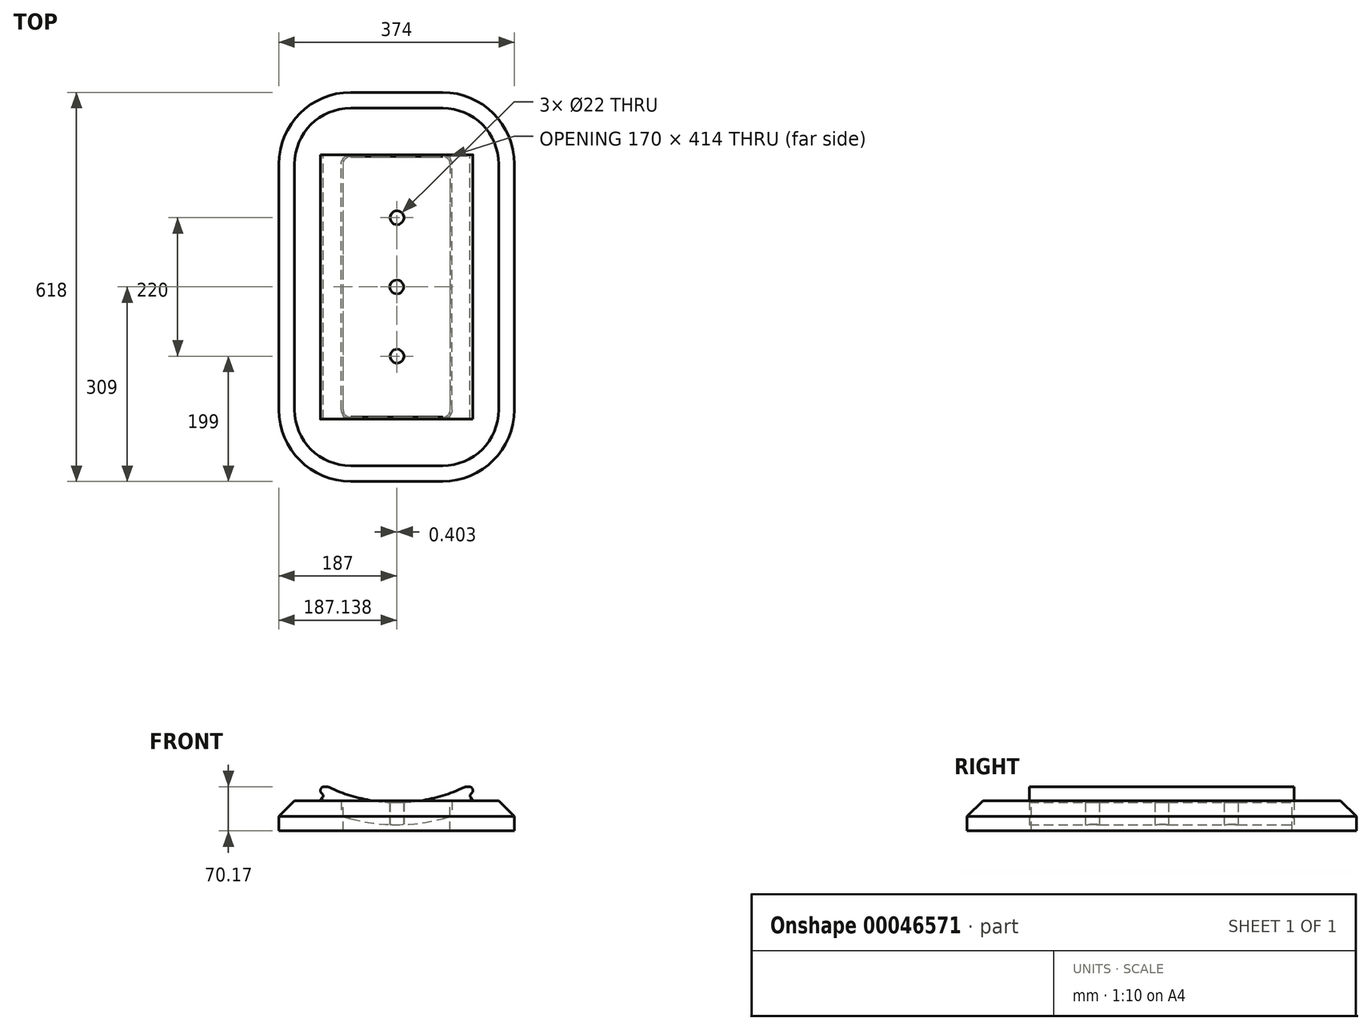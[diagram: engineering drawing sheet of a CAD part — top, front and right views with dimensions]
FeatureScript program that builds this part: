
annotation { "Feature Type Name" : "Feature", "Feature Type Description" : "" }
export const myFeature = defineFeature(function(context is Context, id is Id, definition is map)
    precondition{}
    {
        {
            var Q0;
            Q0=qCreatedBy(makeId("Front.planeOp"),FACE);
            var sketch = newSketch(context, id + "F0", { "sketchPlane" : qUnion([Q0])});
            skArc(sketch, "E0", {"start": v(0, -251.5) * mm, "mid": v(55, -245.41) * mm, "end": v(107.33, -227.45) * mm});
            skLineSegment(sketch, "E1", {"start": v(0, 0) * mm, "end": v(0, -251.5) * mm, "construction": true});
            skLineSegment(sketch, "E2", {"start": v(88, -248.66) * mm, "end": v(88, -272.86) * mm});
            skArc(sketch, "E3", {"start": v(0, -286.7) * mm, "mid": v(44.54, -283.22) * mm, "end": v(88, -272.86) * mm});
            skLineSegment(sketch, "E4", {"start": v(88, -248.66) * mm, "end": v(121, -248.66) * mm});
            skLineSegment(sketch, "E5", {"start": v(121, -248.66) * mm, "end": v(117.68, -243.92) * mm});
            skLineSegment(sketch, "E6", {"start": v(118.25, -237.52) * mm, "end": v(119.62, -236.15) * mm});
            skLineSegment(sketch, "E7", {"start": v(120.65, -230.6) * mm, "end": v(120.16, -229.47) * mm});
            skLineSegment(sketch, "E8", {"start": v(115.58, -226.5) * mm, "end": v(111.6, -226.5) * mm});
            skPoint(sketch, "E9.visualSharp", {"position": v(118.84, -226.5) * mm});
            skArc(sketch, "E9.filletArc", {"start": v(120.16, -229.47) * mm, "mid": v(118.31, -227.3) * mm, "end": v(115.58, -226.5) * mm});
            skPoint(sketch, "E10.visualSharp", {"position": v(122.04, -233.73) * mm});
            skArc(sketch, "E10.filletArc", {"start": v(119.62, -236.15) * mm, "mid": v(121, -233.53) * mm, "end": v(120.65, -230.6) * mm});
            skPoint(sketch, "E11.visualSharp", {"position": v(115.28, -240.48) * mm});
            skArc(sketch, "E11.filletArc", {"start": v(118.25, -237.52) * mm, "mid": v(116.8, -240.62) * mm, "end": v(117.68, -243.92) * mm});
            skLineSegment(sketch, "E12", {"start": v(0, -251.5) * mm, "end": v(0, -286.7) * mm, "construction": true});
            skPoint(sketch, "E13.visualSharp", {"position": v(109.34, -226.5) * mm});
            skArc(sketch, "E13.filletArc", {"start": v(111.6, -226.5) * mm, "mid": v(109.41, -226.73) * mm, "end": v(107.33, -227.45) * mm});
            skArc(sketch, "E14.MirrorCS", {"start": v(0, -251.5) * mm, "mid": v(-55, -245.41) * mm, "end": v(-107.33, -227.45) * mm});
            skArc(sketch, "E15.MirrorCS", {"start": v(-120.16, -229.47) * mm, "mid": v(-118.31, -227.3) * mm, "end": v(-115.58, -226.5) * mm});
            skArc(sketch, "E16.MirrorCS", {"start": v(-119.62, -236.15) * mm, "mid": v(-121, -233.53) * mm, "end": v(-120.65, -230.6) * mm});
            skLineSegment(sketch, "E17.MirrorCS", {"start": v(-115.58, -226.5) * mm, "end": v(-111.6, -226.5) * mm});
            skLineSegment(sketch, "E18.MirrorCS", {"start": v(-118.25, -237.52) * mm, "end": v(-119.62, -236.15) * mm});
            skLineSegment(sketch, "E19.MirrorCS", {"start": v(-120.65, -230.6) * mm, "end": v(-120.16, -229.47) * mm});
            skArc(sketch, "E20.MirrorCS", {"start": v(-111.6, -226.5) * mm, "mid": v(-109.41, -226.73) * mm, "end": v(-107.33, -227.45) * mm});
            skArc(sketch, "E21.MirrorCS", {"start": v(-118.25, -237.52) * mm, "mid": v(-116.8, -240.62) * mm, "end": v(-117.68, -243.92) * mm});
            skLineSegment(sketch, "E22.MirrorCS", {"start": v(-121, -248.66) * mm, "end": v(-117.68, -243.92) * mm});
            skPoint(sketch, "E23.MirrorP", {"position": v(-109.34, -226.5) * mm});
            skPoint(sketch, "E24.MirrorP", {"position": v(-115.28, -240.48) * mm});
            skLineSegment(sketch, "E25.MirrorCS", {"start": v(-88, -248.66) * mm, "end": v(-88, -272.86) * mm});
            skPoint(sketch, "E26.MirrorP", {"position": v(-122.04, -233.73) * mm});
            skLineSegment(sketch, "E27.MirrorCS", {"start": v(-88, -248.66) * mm, "end": v(-121, -248.66) * mm});
            skPoint(sketch, "E28.MirrorP", {"position": v(-118.84, -226.5) * mm});
            skArc(sketch, "E29.MirrorCS", {"start": v(0, -286.7) * mm, "mid": v(-44.54, -283.22) * mm, "end": v(-88, -272.86) * mm});
            skSolve(sketch);
        }
        {
            var Q0;
            Q0=qSketchRegion(id+"F0",true);
            extrude(context, id + "F1", {"entities" : qUnion([Q0]), "depth" : 420 * mm});
        }
        {
            var Q0;
            Q0=makeQuery(id+"F1.opExtrude","CAP_EDGE",EDGE,{"disambiguationData":[OSD([sQuery(id+"F0.wireOp",EDGE,"E2")])],"isStart":false});
            var Q1;
            Q1=makeQuery(id+"F1.opExtrude","CAP_EDGE",EDGE,{"disambiguationData":[OSD([sQuery(id+"F0.wireOp",EDGE,"E25.MirrorCS")])],"isStart":false});
            var Q2;
            Q2=makeQuery(id+"F1.opExtrude","CAP_EDGE",EDGE,{"disambiguationData":[OSD([sQuery(id+"F0.wireOp",EDGE,"E2")])],"isStart":true});
            var Q3;
            Q3=makeQuery(id+"F1.opExtrude","CAP_EDGE",EDGE,{"disambiguationData":[OSD([sQuery(id+"F0.wireOp",EDGE,"E25.MirrorCS")])],"isStart":true});
            fillet(context, id + "F2", {"entities" : qUnion([Q0, Q1, Q2, Q3]), "radius" : 15 * mm, "tangentPropagation" : true, "allowEdgeOverflow" : false});
        }
        {
            var Q0;
            Q0=qCreatedBy(makeId("Top.planeOp"),FACE);
            cPlane(context, id + "F3", {"entities" : qUnion([Q0]), "cplaneType" : CPlaneType.OFFSET, "offset" : 500 * mm, "oppositeDirection" : true, "width" : 150 * mm, "height" : 150 * mm});
        }
        {
            var Q0;
            Q0=qCreatedBy(id+"F3.planeOp",FACE);
            var sketch = newSketch(context, id + "F4", { "sketchPlane" : qUnion([Q0])});
            skLineSegment(sketch, "E30", {"start": v(0, 0) * mm, "end": v(0, -420.24) * mm, "construction": true});
            skLineSegment(sketch, "E31", {"start": v(-86.52, -100) * mm, "end": v(87.6, -100) * mm, "construction": true});
            skLineSegment(sketch, "E32", {"start": v(-34.96, -420.24) * mm, "end": v(21.89, -420.24) * mm, "construction": true});
            skLineSegment(sketch, "E33", {"start": v(-40.22, -210) * mm, "end": v(40.5, -210) * mm, "construction": true});
            skCircle(sketch, "E34", {"center": v(0.54, -100) * mm, "radius": 11 * mm});
            skCircle(sketch, "E35", {"center": v(0.14, -210) * mm, "radius": 11 * mm});
            skCircle(sketch, "E36.MirrorC", {"center": v(0.54, -320) * mm, "radius": 11 * mm});
            skSolve(sketch);
        }
        {
            var Q0;
            Q0=qSketchRegion(id+"F4",true);
            extrude(context, id + "F5", {"entities" : qUnion([Q0]), "operationType" : NewBodyOperationType.REMOVE, "depth" : 267.3 * mm});
        }
        {
            var Q0;
            Q0=makeQuery(id+"F1.opExtrude","SWEPT_FACE",FACE,{"disambiguationData":[OSD([sQuery(id+"F0.wireOp",EDGE,"E27.MirrorCS")])]});
            var sketch = newSketch(context, id + "F6", { "sketchPlane" : qUnion([Q0])});
            skArc(sketch, "E37.0", {"start": v(-85, 15) * mm, "mid": v(-81.49, 6.51) * mm, "end": v(-73, 3) * mm});
            skLineSegment(sketch, "E37.1", {"start": v(-85, 405) * mm, "end": v(-85, 15) * mm});
            skLineSegment(sketch, "E37.2", {"start": v(-73, 3) * mm, "end": v(73, 3) * mm});
            skArc(sketch, "E37.3", {"start": v(-73, 417) * mm, "mid": v(-81.49, 413.49) * mm, "end": v(-85, 405) * mm});
            skArc(sketch, "E37.4", {"start": v(73, 3) * mm, "mid": v(81.49, 6.51) * mm, "end": v(85, 15) * mm});
            skLineSegment(sketch, "E37.5", {"start": v(85, 15) * mm, "end": v(85, 405) * mm});
            skArc(sketch, "E37.6", {"start": v(85, 405) * mm, "mid": v(81.49, 413.49) * mm, "end": v(73, 417) * mm});
            skLineSegment(sketch, "E37.7", {"start": v(73, 417) * mm, "end": v(-73, 417) * mm});
            skArc(sketch, "E38.0", {"start": v(-187, 15) * mm, "mid": v(-153.61, -65.61) * mm, "end": v(-73, -99) * mm});
            skLineSegment(sketch, "E38.1", {"start": v(-187, 405) * mm, "end": v(-187, 15) * mm});
            skLineSegment(sketch, "E38.2", {"start": v(-73, -99) * mm, "end": v(73, -99) * mm});
            skArc(sketch, "E38.3", {"start": v(-73, 519) * mm, "mid": v(-153.61, 485.61) * mm, "end": v(-187, 405) * mm});
            skArc(sketch, "E38.4", {"start": v(73, -99) * mm, "mid": v(153.61, -65.61) * mm, "end": v(187, 15) * mm});
            skLineSegment(sketch, "E38.5", {"start": v(187, 15) * mm, "end": v(187, 405) * mm});
            skArc(sketch, "E38.6", {"start": v(187, 405) * mm, "mid": v(153.61, 485.61) * mm, "end": v(73, 519) * mm});
            skLineSegment(sketch, "E38.7", {"start": v(73, 519) * mm, "end": v(-73, 519) * mm});
            skSolve(sketch);
        }
        {
            var Q0;
            Q0=makeQuery(id+"F6.imprint","IMPRINT",FACE,{"disambiguationData":[TD([[makeQuery(id+"F6.imprint","IMPRINT",EDGE,{"derivedFrom":sQuery(id+"F6.wireOp",EDGE,"E37.0")}),-1.0]])]});
            var Q1;
            {var subQ0=sQuery(id+"F0.wireOp",EDGE,"E27.MirrorCS");Q1=makeQuery(id+"F6.imprint","IMPRINT",FACE,{"disambiguationData":[TD([[makeQuery(id+"F6.imprint","IMPRINT",EDGE,{"derivedFrom":makeQuery(id+"F1.opExtrude","CAP_EDGE",EDGE,{"disambiguationData":[OSD([subQ0])],"isStart":true})}),-1.0]])]});}
            extrude(context, id + "F7", {"entities" : qUnion([Q0, Q1]), "depth" : 48 * mm});
        }
        {
            var Q0;
            Q0=makeQuery(id+"F7.opExtrude","CAP_EDGE",EDGE,{"disambiguationData":[OSD([sQuery(id+"F6.wireOp",EDGE,"E38.7")])],"isStart":true});
            chamfer(context, id + "F8", {"entities" : qUnion([Q0]), "width" : 25 * mm, "tangentPropagation" : true});
        }
    });
